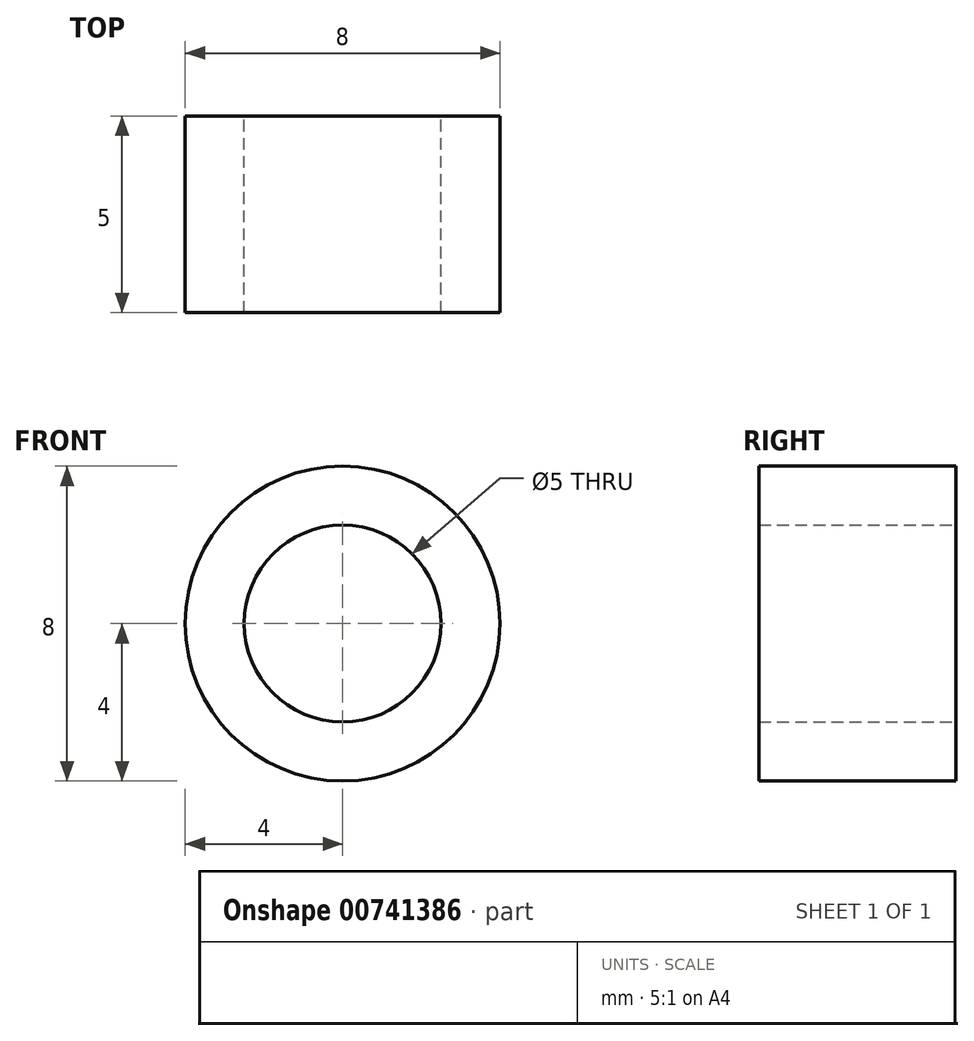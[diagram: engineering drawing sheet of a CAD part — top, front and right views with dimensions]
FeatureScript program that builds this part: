
annotation { "Feature Type Name" : "Feature", "Feature Type Description" : "" }
export const myFeature = defineFeature(function(context is Context, id is Id, definition is map)
    precondition{}
    {
        {
            var Q0;
            Q0=qCreatedBy(makeId("Front.planeOp"),FACE);
            var sketch = newSketch(context, id + "F0", { "sketchPlane" : qUnion([Q0])});
            skCircle(sketch, "E0", {"center": v(0, 0) * mm, "radius": 4 * mm});
            skCircle(sketch, "E1", {"center": v(0, 0) * mm, "radius": 2.5 * mm});
            skSolve(sketch);
        }
        {
            var Q0;
            Q0=makeQuery(id+"F0.imprint","IMPRINT",FACE,{"disambiguationData":[TD([[makeQuery(id+"F0.imprint","IMPRINT",EDGE,{"derivedFrom":sQuery(id+"F0.wireOp",EDGE,"E0")}),1.0]])]});
            extrude(context, id + "F1", {"entities" : qUnion([Q0]), "depth" : 5 * mm, "offsetDistance" : 25 * mm});
        }
    });
